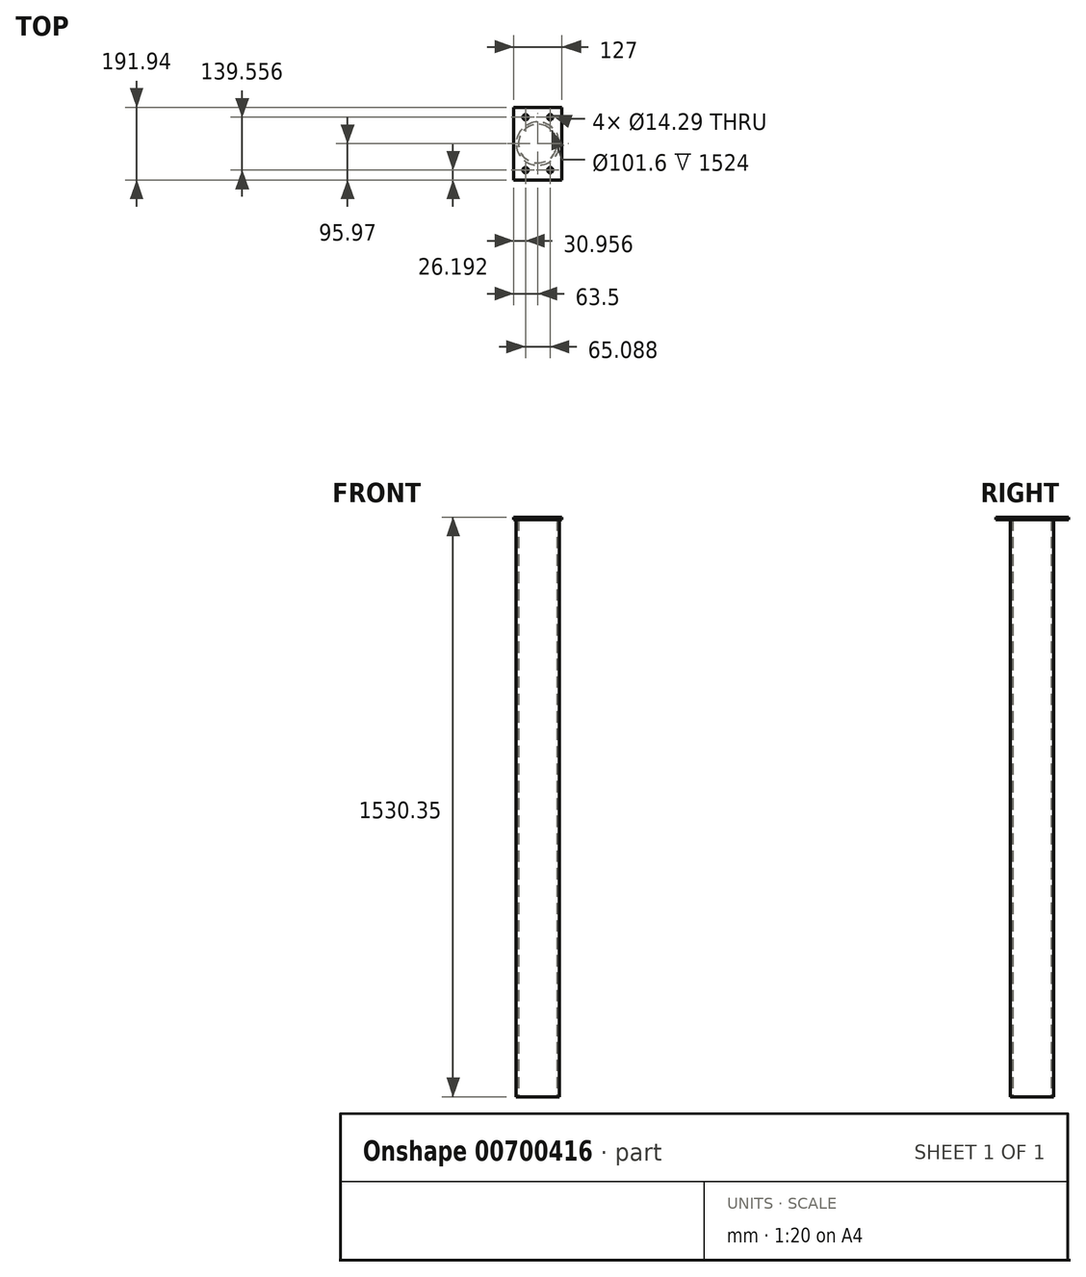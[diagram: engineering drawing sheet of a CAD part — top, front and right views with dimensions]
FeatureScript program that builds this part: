
annotation { "Feature Type Name" : "Feature", "Feature Type Description" : "" }
export const myFeature = defineFeature(function(context is Context, id is Id, definition is map)
    precondition{}
    {
        {
            var Q0;
            Q0=qCreatedBy(makeId("Top.planeOp"),FACE);
            var sketch = newSketch(context, id + "F0", { "sketchPlane" : qUnion([Q0])});
            skCircle(sketch, "E0", {"center": v(0, 0) * mm, "radius": 50.8 * mm});
            skCircle(sketch, "E1", {"center": v(0, 0) * mm, "radius": 57.15 * mm});
            skSolve(sketch);
        }
        {
            var Q0;
            Q0 = qSketchRegion(id + "F0", true);
            extrude(context, id + "F1", {"entities" : qUnion([Q0]), "depth" : 1524 * mm, "offsetDistance" : 25.4 * mm});
        }
        {
            var Q0;
            Q0=makeQuery(id+"F1.opExtrude","CAP_FACE",FACE,{"disambiguationData":[OSD([sQuery(id+"F0.wireOp",EDGE,"E0"),sQuery(id+"F0.wireOp",EDGE,"E1")])],"isStart":false});
            var sketch = newSketch(context, id + "F2", { "sketchPlane" : qUnion([Q0])});
            skLineSegment(sketch, "E2.bottom", {"start": v(-63.5, 95.97) * mm, "end": v(63.5, 95.97) * mm});
            skLineSegment(sketch, "E2.top", {"start": v(-63.5, -95.97) * mm, "end": v(63.5, -95.97) * mm});
            skLineSegment(sketch, "E2.left", {"start": v(-63.5, 95.97) * mm, "end": v(-63.5, -95.97) * mm});
            skLineSegment(sketch, "E2.right", {"start": v(63.5, 95.97) * mm, "end": v(63.5, -95.97) * mm});
            skLineSegment(sketch, "E3", {"start": v(-63.5, 95.97) * mm, "end": v(63.5, -95.97) * mm, "construction": true});
            skCircle(sketch, "E4", {"center": v(-32.54, 69.78) * mm, "radius": 7.14 * mm});
            skCircle(sketch, "E5", {"center": v(32.54, 69.78) * mm, "radius": 7.14 * mm});
            skCircle(sketch, "E6", {"center": v(-32.54, -69.78) * mm, "radius": 7.14 * mm});
            skCircle(sketch, "E7", {"center": v(32.54, -69.78) * mm, "radius": 7.14 * mm});
            skCircle(sketch, "E8", {"center": v(0, 0) * mm, "radius": 57.15 * mm, "construction": true});
            skSolve(sketch);
        }
        {
            var Q0;
            Q0 = qSketchRegion(id + "F2", true);
            extrude(context, id + "F3", {"entities" : qUnion([Q0]), "operationType" : NewBodyOperationType.ADD, "depth" : 6.35 * mm, "offsetDistance" : 25.4 * mm});
        }
    });
